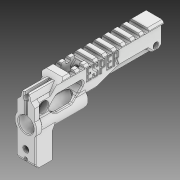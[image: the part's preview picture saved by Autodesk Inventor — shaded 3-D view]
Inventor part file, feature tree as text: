
AUTODESK INVENTOR PART (.ipt)
format: ipt  version: 2020 (Build 240168000, 168)  size: 905,216 bytes
history: native  units: in
note: dims shown in document units (in); Inventor stores cm internally (conversion verified against a paired STEP export)
features: extrude x5, sketch x5, chamfer x2, projected_geometry x1, imported_body x1
ambient origin geometry x8: Origin, YZ Plane, XZ Plane, XY Plane, X Axis, Y Axis, Z Axis, Center Point
bodies: Solid1 (feature_tree)
feature tree (14):
  extrude  "Extrusion1"  Depth=0.0394in TaperAngle=45.0deg
  chamfer  "Chamfer1"  [1 undecoded]
  extrude  "Extrusion2"  Depth=0.3937in TaperAngle=0.0deg
  chamfer  "Chamfer2"  [1 undecoded]
  extrude  "Extrusion3"  Depth=0.1887in TaperAngle=0.0deg
  extrude  "Extrusion4"  [1 undecoded]
  extrude  "Extrusion5"  [1 undecoded]
  sketch  "Sketch1"  dims[d0=0.0in d1=0.0in d2=0.0394in d3=0.0787in d4=45.0deg]
  sketch  "Sketch2"  dims[d6=0.1425in d7=0.0in d8=0.0in]
  sketch  "Sketch3"  dims[d9=0.0394in d10=0.0787in d11=45.0deg d12=0.3937in d13=0.0in]
  sketch  "Sketch4"  dims[d14=0.1378in]
  sketch  "Sketch5"  dims[d15=1.2598in d16=0.0in d17=0.0in d18=0.1887in d19=0.0in]
  projected_geometry  "Projected Loop1"
  imported_body  "Base1"
note: 4 required parameter values undecoded (feature->parameter linkage not recoverable at this tier; creation-order binding heuristic only, values carry confidence <= 0.55)
